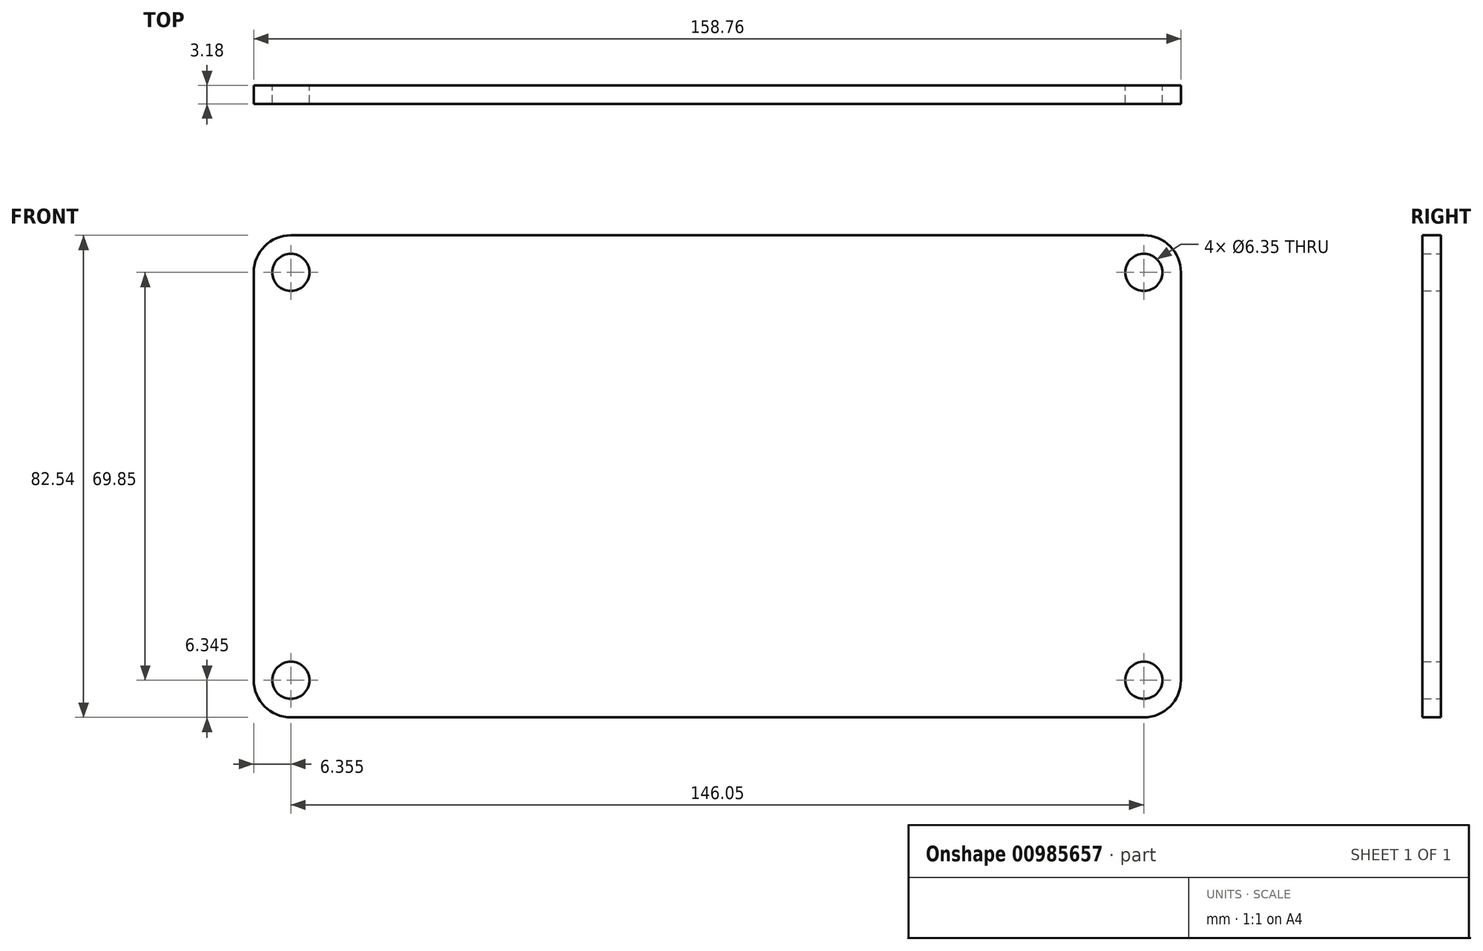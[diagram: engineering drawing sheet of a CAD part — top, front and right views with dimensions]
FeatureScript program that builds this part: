
annotation { "Feature Type Name" : "Feature", "Feature Type Description" : "" }
export const myFeature = defineFeature(function(context is Context, id is Id, definition is map)
    precondition{}
    {
        {
            var Q0;
            Q0=qCreatedBy(makeId("Front.planeOp"),FACE);
            var sketch = newSketch(context, id + "F0", { "sketchPlane" : qUnion([Q0])});
            skLineSegment(sketch, "E0.bottom", {"start": v(73.02, 41.28) * mm, "end": v(-73.03, 41.28) * mm});
            skLineSegment(sketch, "E0.top", {"start": v(73.03, -41.28) * mm, "end": v(-73.03, -41.28) * mm});
            skLineSegment(sketch, "E0.left", {"start": v(79.38, 34.92) * mm, "end": v(79.38, -34.93) * mm});
            skLineSegment(sketch, "E0.right", {"start": v(-79.38, 34.93) * mm, "end": v(-79.38, -34.93) * mm});
            skPoint(sketch, "E0.middle", {"position": v(0, 0) * mm});
            skPoint(sketch, "E1.visualSharp", {"position": v(-79.38, 41.28) * mm});
            skArc(sketch, "E1.filletArc", {"start": v(-73.03, 41.28) * mm, "mid": v(-77.52, 39.42) * mm, "end": v(-79.38, 34.93) * mm});
            skPoint(sketch, "E2.visualSharp", {"position": v(-79.38, -41.28) * mm});
            skArc(sketch, "E2.filletArc", {"start": v(-79.38, -34.93) * mm, "mid": v(-77.52, -39.42) * mm, "end": v(-73.03, -41.28) * mm});
            skPoint(sketch, "E3.visualSharp", {"position": v(79.38, -41.28) * mm});
            skArc(sketch, "E3.filletArc", {"start": v(73.03, -41.28) * mm, "mid": v(77.52, -39.42) * mm, "end": v(79.38, -34.93) * mm});
            skPoint(sketch, "E4.visualSharp", {"position": v(79.38, 41.28) * mm});
            skArc(sketch, "E4.filletArc", {"start": v(79.38, 34.92) * mm, "mid": v(77.52, 39.42) * mm, "end": v(73.02, 41.28) * mm});
            skCircle(sketch, "E5", {"center": v(-73.03, 34.93) * mm, "radius": 3.18 * mm});
            skCircle(sketch, "E6.MirrorC", {"center": v(-73.03, -34.93) * mm, "radius": 3.18 * mm});
            skCircle(sketch, "E7.MirrorC", {"center": v(73.03, -34.93) * mm, "radius": 3.18 * mm});
            skCircle(sketch, "E8.MirrorC", {"center": v(73.03, 34.93) * mm, "radius": 3.18 * mm});
            skSolve(sketch);
        }
        {
            var Q0;
            Q0=makeQuery(id+"F0.imprint","IMPRINT",FACE,{"disambiguationData":[TD([[makeQuery(id+"F0.imprint","IMPRINT",EDGE,{"derivedFrom":sQuery(id+"F0.wireOp",EDGE,"E0.bottom")}),1.0]])]});
            extrude(context, id + "F1", {"entities" : qUnion([Q0]), "depth" : 3.17 * mm, "offsetDistance" : 25.4 * mm});
        }
    });
